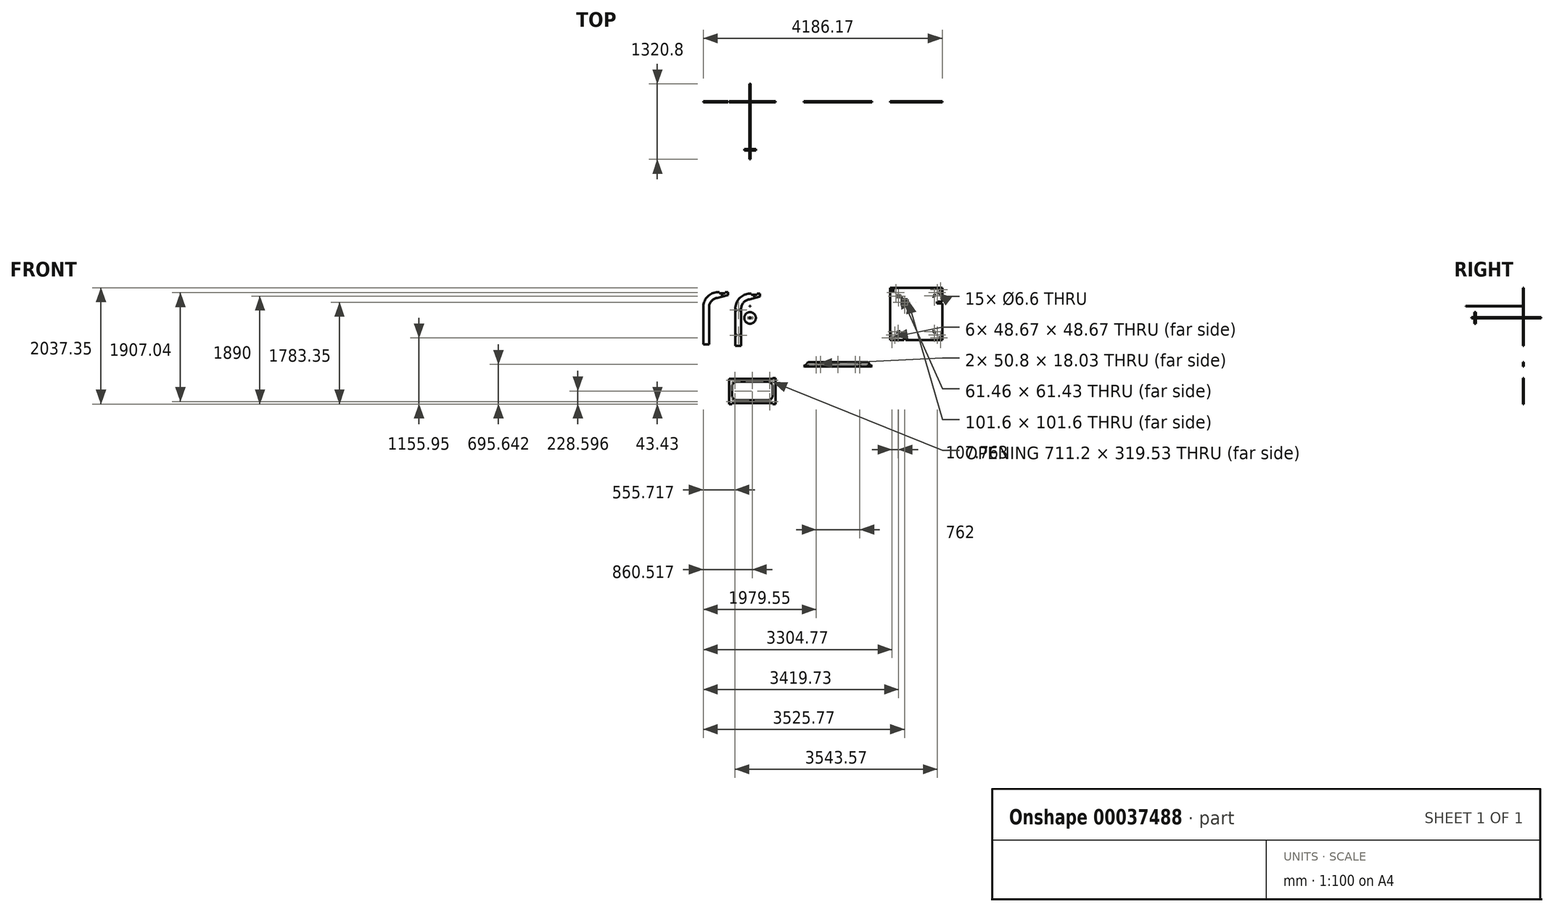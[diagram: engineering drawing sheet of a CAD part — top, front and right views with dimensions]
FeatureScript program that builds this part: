
annotation { "Feature Type Name" : "Feature", "Feature Type Description" : "" }
export const myFeature = defineFeature(function(context is Context, id is Id, definition is map)
    precondition{}
    {
        {
            var Q0;
            Q0=qCreatedBy(makeId("Front.planeOp"),FACE);
            var sketch = newSketch(context, id + "F0", { "sketchPlane" : qUnion([Q0])});
            skPoint(sketch, "E0.endSnap0", {"position": v(175.05, 374.22) * mm});
            skLineSegment(sketch, "E1", {"start": v(-256.75, -489.38) * mm, "end": v(-256.75, 159.86) * mm});
            skLineSegment(sketch, "E2", {"start": v(-13.2, 324.52) * mm, "end": v(175.05, 374.69) * mm});
            skLineSegment(sketch, "E3", {"start": v(-256.75, -489.38) * mm, "end": v(-155.15, -489.38) * mm});
            skArc(sketch, "E4.0", {"start": v(-13.2, 324.52) * mm, "mid": v(-114.76, 268.56) * mm, "end": v(-155.15, 159.86) * mm});
            skLineSegment(sketch, "E5", {"start": v(-155.15, -489.38) * mm, "end": v(-155.15, 159.86) * mm});
            skArc(sketch, "E6", {"start": v(-28.15, 425.02) * mm, "mid": v(-191.71, 334.9) * mm, "end": v(-256.75, 159.86) * mm});
            skLineSegment(sketch, "E0", {"start": v(-28.15, 374.69) * mm, "end": v(175.05, 374.69) * mm, "construction": true});
            skLineSegment(sketch, "E7", {"start": v(175.05, 406.98) * mm, "end": v(175.05, 341.45) * mm, "construction": true});
            skLineSegment(sketch, "E8", {"start": v(-28.15, 425.02) * mm, "end": v(22.65, 425.02) * mm});
            skLineSegment(sketch, "E9", {"start": v(175.05, 406.98) * mm, "end": v(175.05, 374.22) * mm});
            skLineSegment(sketch, "E10", {"start": v(22.65, 406.98) * mm, "end": v(124.25, 406.98) * mm});
            skLineSegment(sketch, "E11", {"start": v(175.05, 425.02) * mm, "end": v(175.05, 406.98) * mm});
            skLineSegment(sketch, "E12.MirrorCS", {"start": v(175.05, 425.02) * mm, "end": v(124.25, 425.02) * mm});
            skLineSegment(sketch, "E13", {"start": v(22.65, 425.02) * mm, "end": v(22.65, 406.98) * mm});
            skLineSegment(sketch, "E14.MirrorCS", {"start": v(124.25, 425.02) * mm, "end": v(124.25, 406.98) * mm});
            skLineSegment(sketch, "E15", {"start": v(-205.95, -489.38) * mm, "end": v(-205.95, -311.58) * mm, "construction": true});
            skPoint(sketch, "E15.endSnap0", {"position": v(-205.95, -489.38) * mm});
            skLineSegment(sketch, "E16.bottom", {"start": v(-256.75, 145.62) * mm, "end": v(-231.35, 145.62) * mm});
            skLineSegment(sketch, "E16.top", {"start": v(-256.75, 127.58) * mm, "end": v(-231.35, 127.58) * mm});
            skLineSegment(sketch, "E16.left", {"start": v(-256.75, 145.62) * mm, "end": v(-256.75, 127.58) * mm});
            skPoint(sketch, "E17.endSnap0", {"position": v(-388.49, 397.96) * mm});
            skArc(sketch, "E18.0", {"start": v(-576.73, 348.27) * mm, "mid": v(-678.3, 292.31) * mm, "end": v(-718.69, 183.6) * mm});
            skArc(sketch, "E19", {"start": v(-591.69, 448.76) * mm, "mid": v(-755.25, 358.65) * mm, "end": v(-820.29, 183.6) * mm});
            skLineSegment(sketch, "E20", {"start": v(-820.29, -465.64) * mm, "end": v(-820.29, 183.6) * mm});
            skPoint(sketch, "E21.endSnap0", {"position": v(-849.05, 398.3) * mm});
            skLineSegment(sketch, "E22", {"start": v(-718.69, -465.64) * mm, "end": v(-718.69, 183.6) * mm});
            skLineSegment(sketch, "E23", {"start": v(-576.73, 348.27) * mm, "end": v(-388.49, 398.43) * mm});
            skPoint(sketch, "E24.MirrorP", {"position": v(-490.09, 418.36) * mm});
            skLineSegment(sketch, "E25", {"start": v(-820.29, -465.64) * mm, "end": v(-718.69, -465.64) * mm});
            skLineSegment(sketch, "E17", {"start": v(-591.69, 398.43) * mm, "end": v(-388.49, 398.43) * mm, "construction": true});
            skLineSegment(sketch, "E26", {"start": v(-540.89, 430.73) * mm, "end": v(-439.29, 430.73) * mm});
            skLineSegment(sketch, "E27", {"start": v(-540.89, 448.76) * mm, "end": v(-540.89, 430.73) * mm});
            skLineSegment(sketch, "E28", {"start": v(-591.69, 448.76) * mm, "end": v(-540.89, 448.76) * mm});
            skLineSegment(sketch, "E29", {"start": v(-388.49, 448.76) * mm, "end": v(-388.49, 430.73) * mm});
            skLineSegment(sketch, "E30.MirrorCS", {"start": v(-388.49, 448.76) * mm, "end": v(-439.29, 448.76) * mm});
            skLineSegment(sketch, "E31", {"start": v(-388.49, 430.73) * mm, "end": v(-388.49, 365.2) * mm, "construction": true});
            skLineSegment(sketch, "E32", {"start": v(-388.49, 430.73) * mm, "end": v(-388.49, 397.96) * mm});
            skLineSegment(sketch, "E33.MirrorCS", {"start": v(-439.29, 448.76) * mm, "end": v(-439.29, 430.73) * mm});
            skCircle(sketch, "E34", {"center": v(-490.09, 405.33) * mm, "radius": 5.59 * mm});
            skLineSegment(sketch, "E35", {"start": v(-490.09, 399.74) * mm, "end": v(-490.09, 430.73) * mm, "construction": true});
            skLineSegment(sketch, "E36", {"start": v(-490.09, 398.43) * mm, "end": v(-490.09, 440.42) * mm, "construction": true});
            skLineSegment(sketch, "E37", {"start": v(-205.95, -489.38) * mm, "end": v(-205.95, -362.38) * mm, "construction": true});
            skLineSegment(sketch, "E38", {"start": v(-205.95, 76.78) * mm, "end": v(-205.95, -344.35) * mm, "construction": true});
            skCircle(sketch, "E39", {"center": v(73.45, 381.58) * mm, "radius": 5.59 * mm});
            skLineSegment(sketch, "E40", {"start": v(73.45, 376) * mm, "end": v(73.45, 406.98) * mm, "construction": true});
            skPoint(sketch, "E41", {"position": v(73.45, 406.98) * mm});
            skLineSegment(sketch, "E42.bottom", {"start": v(-366.17, -1069.77) * mm, "end": v(446.63, -1069.77) * mm});
            skLineSegment(sketch, "E42.top", {"start": v(-366.17, -1490.9) * mm, "end": v(446.63, -1490.9) * mm});
            skLineSegment(sketch, "E42.left", {"start": v(-366.17, -1069.77) * mm, "end": v(-366.17, -1490.9) * mm});
            skLineSegment(sketch, "E42.right", {"start": v(446.63, -1069.77) * mm, "end": v(446.63, -1490.9) * mm});
            skLineSegment(sketch, "E43.bottom", {"start": v(-366.17, -1069.77) * mm, "end": v(-315.37, -1069.77) * mm});
            skLineSegment(sketch, "E43.top", {"start": v(-366.17, -1051.73) * mm, "end": v(-315.37, -1051.73) * mm});
            skLineSegment(sketch, "E43.left", {"start": v(-366.17, -1069.77) * mm, "end": v(-366.17, -1051.73) * mm});
            skLineSegment(sketch, "E43.right", {"start": v(-315.37, -1069.77) * mm, "end": v(-315.37, -1051.73) * mm});
            skLineSegment(sketch, "E44", {"start": v(40.23, -1069.77) * mm, "end": v(40.23, -1490.9) * mm, "construction": true});
            skLineSegment(sketch, "E45", {"start": v(40.23, -1490.9) * mm, "end": v(446.63, -1280.33) * mm, "construction": true});
            skLineSegment(sketch, "E46", {"start": v(446.63, -1280.33) * mm, "end": v(-366.17, -1280.33) * mm, "construction": true});
            skLineSegment(sketch, "E47.MirrorCS", {"start": v(395.83, -1069.77) * mm, "end": v(395.83, -1051.73) * mm});
            skLineSegment(sketch, "E48.MirrorCS", {"start": v(446.63, -1069.77) * mm, "end": v(395.83, -1069.77) * mm});
            skLineSegment(sketch, "E49.MirrorCS", {"start": v(446.63, -1051.73) * mm, "end": v(395.83, -1051.73) * mm});
            skLineSegment(sketch, "E50.MirrorCS", {"start": v(446.63, -1069.77) * mm, "end": v(446.63, -1051.73) * mm});
            skLineSegment(sketch, "E51.MirrorCS", {"start": v(446.63, -1490.9) * mm, "end": v(446.63, -1508.93) * mm});
            skLineSegment(sketch, "E52.MirrorCS", {"start": v(-315.37, -1490.9) * mm, "end": v(-315.37, -1508.93) * mm});
            skLineSegment(sketch, "E53.MirrorCS", {"start": v(395.83, -1490.9) * mm, "end": v(395.83, -1508.93) * mm});
            skLineSegment(sketch, "E54.MirrorCS", {"start": v(-366.17, -1490.9) * mm, "end": v(-366.17, -1508.93) * mm});
            skLineSegment(sketch, "E55.MirrorCS", {"start": v(-366.17, -1508.93) * mm, "end": v(-315.37, -1508.93) * mm});
            skLineSegment(sketch, "E56.MirrorCS", {"start": v(446.63, -1490.9) * mm, "end": v(395.83, -1490.9) * mm});
            skLineSegment(sketch, "E57.MirrorCS", {"start": v(-366.17, -1490.9) * mm, "end": v(-315.37, -1490.9) * mm});
            skLineSegment(sketch, "E58.MirrorCS", {"start": v(446.63, -1508.93) * mm, "end": v(395.83, -1508.93) * mm});
            skLineSegment(sketch, "E59.bottom", {"start": v(-239.17, -1120.57) * mm, "end": v(319.63, -1120.57) * mm});
            skLineSegment(sketch, "E59.top", {"start": v(-239.17, -1440.1) * mm, "end": v(319.63, -1440.1) * mm});
            skLineSegment(sketch, "E59.left", {"start": v(-315.37, -1196.77) * mm, "end": v(-315.37, -1363.9) * mm});
            skLineSegment(sketch, "E59.right", {"start": v(395.83, -1196.77) * mm, "end": v(395.83, -1363.9) * mm});
            skPoint(sketch, "E60.visualSharp", {"position": v(-315.37, -1120.57) * mm});
            skArc(sketch, "E60.filletArc", {"start": v(-239.17, -1120.57) * mm, "mid": v(-293.05, -1142.89) * mm, "end": v(-315.37, -1196.77) * mm});
            skPoint(sketch, "E61.visualSharp", {"position": v(395.83, -1120.57) * mm});
            skArc(sketch, "E61.filletArc", {"start": v(395.83, -1196.77) * mm, "mid": v(373.5, -1142.89) * mm, "end": v(319.63, -1120.57) * mm});
            skPoint(sketch, "E62.visualSharp", {"position": v(395.83, -1440.1) * mm});
            skArc(sketch, "E62.filletArc", {"start": v(319.63, -1440.1) * mm, "mid": v(373.5, -1417.78) * mm, "end": v(395.83, -1363.9) * mm});
            skPoint(sketch, "E63.visualSharp", {"position": v(-315.37, -1440.1) * mm});
            skArc(sketch, "E63.filletArc", {"start": v(-315.37, -1363.9) * mm, "mid": v(-293.05, -1417.78) * mm, "end": v(-239.17, -1440.1) * mm});
            skLineSegment(sketch, "E64.right", {"start": v(2756.28, 325.22) * mm, "end": v(2756.28, 223.62) * mm});
            skLineSegment(sketch, "E65", {"start": v(2451.48, 71.22) * mm, "end": v(3365.88, 71.22) * mm, "construction": true});
            skLineSegment(sketch, "E66", {"start": v(3365.88, 71.22) * mm, "end": v(2908.68, 528.42) * mm, "construction": true});
            skLineSegment(sketch, "E67", {"start": v(2451.48, -385.98) * mm, "end": v(3365.88, 528.42) * mm, "construction": true});
            skLineSegment(sketch, "E68.trimOffspring", {"start": v(2728.84, -385.98) * mm, "end": v(3365.88, -385.98) * mm});
            skLineSegment(sketch, "E69.MirrorCS", {"start": v(3365.88, 286.32) * mm, "end": v(3270.63, 286.32) * mm});
            skLineSegment(sketch, "E70.bottom", {"start": v(2451.48, 528.42) * mm, "end": v(3365.88, 528.42) * mm});
            skLineSegment(sketch, "E70.top", {"start": v(2451.48, -385.98) * mm, "end": v(2693.91, -385.98) * mm});
            skLineSegment(sketch, "E71", {"start": v(2451.48, 528.42) * mm, "end": v(2451.48, 528.42) * mm});
            skLineSegment(sketch, "E70.left", {"start": v(2451.48, 528.42) * mm, "end": v(2451.48, -385.98) * mm});
            skLineSegment(sketch, "E70.right", {"start": v(3365.88, 528.42) * mm, "end": v(3365.88, 286.32) * mm});
            skLineSegment(sketch, "E64.top", {"start": v(2654.68, 223.62) * mm, "end": v(2756.28, 223.62) * mm});
            skLineSegment(sketch, "E72.MirrorCS", {"start": v(3270.63, 251.4) * mm, "end": v(3365.88, 251.4) * mm});
            skLineSegment(sketch, "E73", {"start": v(2451.48, 528.42) * mm, "end": v(3365.88, -385.98) * mm, "construction": true});
            skLineSegment(sketch, "E74.trimOffspring", {"start": v(3365.88, 251.4) * mm, "end": v(3365.88, -385.98) * mm});
            skLineSegment(sketch, "E75.right", {"start": v(2693.91, -386.78) * mm, "end": v(2693.91, -291.53) * mm});
            skLineSegment(sketch, "E64.left", {"start": v(2654.68, 325.22) * mm, "end": v(2654.68, 223.62) * mm});
            skPoint(sketch, "E76.orphan", {"position": v(2605.68, 387.29) * mm});
            skLineSegment(sketch, "E77.right", {"start": v(2728.84, -291.53) * mm, "end": v(2728.84, -385.98) * mm});
            skLineSegment(sketch, "E64.bottom", {"start": v(2654.68, 325.22) * mm, "end": v(2756.28, 325.22) * mm});
            skLineSegment(sketch, "E78.MirrorCS", {"start": v(2522.4, 483.62) * mm, "end": v(2486.49, 519.54) * mm});
            skLineSegment(sketch, "E79.MirrorCS", {"start": v(3270.63, 286.32) * mm, "end": v(3270.63, 251.4) * mm});
            skLineSegment(sketch, "E80.MirrorCS", {"start": v(2594.25, 411.78) * mm, "end": v(2630.17, 375.86) * mm});
            skLineSegment(sketch, "E81", {"start": v(2630.17, 375.86) * mm, "end": v(2604.67, 350.36) * mm});
            skLineSegment(sketch, "E82.MirrorCS", {"start": v(2522.4, 483.62) * mm, "end": v(2496.94, 458.08) * mm});
            skLineSegment(sketch, "E83.MirrorCS", {"start": v(2496.94, 458.08) * mm, "end": v(2460.98, 494.04) * mm});
            skLineSegment(sketch, "E84.MirrorCS", {"start": v(2568.71, 386.31) * mm, "end": v(2604.67, 350.36) * mm});
            skLineSegment(sketch, "E77.bottom", {"start": v(2693.91, -291.53) * mm, "end": v(2728.84, -291.53) * mm});
            skCircle(sketch, "E85", {"center": v(2551.8, 441.17) * mm, "radius": 3.3 * mm});
            skLineSegment(sketch, "E86", {"start": v(2594.25, 411.78) * mm, "end": v(2568.71, 386.31) * mm});
            skLineSegment(sketch, "E87", {"start": v(2612.2, 393.82) * mm, "end": v(2599.15, 380.76) * mm, "construction": true});
            skLineSegment(sketch, "E88", {"start": v(2587.7, 405.26) * mm, "end": v(2551.8, 441.17) * mm, "construction": true});
            skLineSegment(sketch, "E89", {"start": v(2551.8, 441.17) * mm, "end": v(2545.27, 434.64) * mm, "construction": true});
            skLineSegment(sketch, "E90.MirrorCS", {"start": v(2486.49, 519.54) * mm, "end": v(2460.98, 494.04) * mm});
            skLineSegment(sketch, "E91.MirrorCS", {"start": v(3212.14, 400.7) * mm, "end": v(3225.15, 387.7) * mm, "construction": true});
            skLineSegment(sketch, "E92.MirrorCS", {"start": v(3308.54, 483.84) * mm, "end": v(3344.47, 519.76) * mm});
            skLineSegment(sketch, "E93.MirrorCS", {"start": v(3236.7, 412) * mm, "end": v(3249.45, 399.24) * mm});
            skLineSegment(sketch, "E94.MirrorCS", {"start": v(3321.3, 471.08) * mm, "end": v(3357.22, 507) * mm});
            skLineSegment(sketch, "E95.MirrorCS", {"start": v(3249.45, 399.24) * mm, "end": v(3213.53, 363.32) * mm});
            skPoint(sketch, "E96.MirrorP", {"position": v(3218.65, 394.2) * mm});
            skLineSegment(sketch, "E97.MirrorCS", {"start": v(3344.47, 519.76) * mm, "end": v(3357.22, 507) * mm});
            skLineSegment(sketch, "E98.MirrorCS", {"start": v(3236.7, 412) * mm, "end": v(3200.78, 376.07) * mm});
            skLineSegment(sketch, "E99.MirrorCS", {"start": v(3200.78, 376.07) * mm, "end": v(3213.53, 363.32) * mm});
            skLineSegment(sketch, "E100.MirrorCS", {"start": v(3308.54, 483.84) * mm, "end": v(3321.3, 471.08) * mm});
            skLineSegment(sketch, "E101", {"start": v(2908.68, 528.42) * mm, "end": v(2908.68, -385.98) * mm, "construction": true});
            skPoint(sketch, "E102", {"position": v(3314.92, 477.46) * mm});
            skLineSegment(sketch, "E103", {"start": v(-532.03, -811.57) * mm, "end": v(-532.06, -805.22) * mm});
            skLineSegment(sketch, "E104.0", {"start": v(-366.17, -1095.17) * mm, "end": v(446.63, -1095.17) * mm, "construction": true});
            skCircle(sketch, "E105", {"center": v(40.23, -1095.17) * mm, "radius": 3.3 * mm});
            skCircle(sketch, "E106", {"center": v(-264.57, -1095.17) * mm, "radius": 3.3 * mm});
            skCircle(sketch, "E107.MirrorC", {"center": v(345.03, -1095.17) * mm, "radius": 3.3 * mm});
            skPoint(sketch, "E108", {"position": v(1184.66, -813.29) * mm});
            skLineSegment(sketch, "E109", {"start": v(949.71, -849.2) * mm, "end": v(2130.8, -849.2) * mm});
            skLineSegment(sketch, "E110", {"start": v(2058.96, -777.37) * mm, "end": v(1021.55, -777.37) * mm});
            skLineSegment(sketch, "E111.bottom", {"start": v(1133.86, -822.3) * mm, "end": v(1184.66, -822.3) * mm});
            skLineSegment(sketch, "E111.top", {"start": v(1133.86, -804.27) * mm, "end": v(1184.66, -804.27) * mm});
            skLineSegment(sketch, "E112", {"start": v(1540.26, -849.2) * mm, "end": v(1540.26, -777.37) * mm, "construction": true});
            skLineSegment(sketch, "E113", {"start": v(949.71, -849.2) * mm, "end": v(1021.55, -777.37) * mm});
            skCircle(sketch, "E114", {"center": v(1235.46, -813.29) * mm, "radius": 3.3 * mm});
            skLineSegment(sketch, "E111.right", {"start": v(1184.66, -822.3) * mm, "end": v(1184.66, -804.27) * mm});
            skLineSegment(sketch, "E111.left", {"start": v(1133.86, -822.3) * mm, "end": v(1133.86, -804.27) * mm});
            skLineSegment(sketch, "E115.MirrorCS", {"start": v(2130.8, -849.2) * mm, "end": v(2058.96, -777.37) * mm});
            skCircle(sketch, "E116.MirrorC", {"center": v(3279, 441.54) * mm, "radius": 3.3 * mm});
            skLineSegment(sketch, "E117", {"start": v(3243.08, 405.62) * mm, "end": v(3314.92, 477.46) * mm, "construction": true});
            skCircle(sketch, "E118.MirrorC", {"center": v(3279, -299.1) * mm, "radius": 3.3 * mm});
            skLineSegment(sketch, "E119.MirrorCS", {"start": v(3236.7, -269.55) * mm, "end": v(3249.45, -256.8) * mm});
            skLineSegment(sketch, "E120.MirrorCS", {"start": v(3344.47, -377.31) * mm, "end": v(3357.22, -364.56) * mm});
            skLineSegment(sketch, "E121.MirrorCS", {"start": v(3308.54, -341.4) * mm, "end": v(3321.3, -328.64) * mm});
            skLineSegment(sketch, "E122.MirrorCS", {"start": v(3200.78, -233.63) * mm, "end": v(3213.53, -220.88) * mm});
            skLineSegment(sketch, "E123.MirrorCS", {"start": v(3243.08, -263.17) * mm, "end": v(3314.92, -335.02) * mm, "construction": true});
            skLineSegment(sketch, "E124.MirrorCS", {"start": v(3212.14, -258.26) * mm, "end": v(3225.15, -245.25) * mm, "construction": true});
            skLineSegment(sketch, "E125.MirrorCS", {"start": v(3321.3, -328.64) * mm, "end": v(3357.22, -364.56) * mm});
            skLineSegment(sketch, "E126.MirrorCS", {"start": v(3236.7, -269.55) * mm, "end": v(3200.78, -233.63) * mm});
            skLineSegment(sketch, "E127.MirrorCS", {"start": v(3308.54, -341.4) * mm, "end": v(3344.47, -377.31) * mm});
            skPoint(sketch, "E128.MirrorP", {"position": v(3218.65, -251.76) * mm});
            skPoint(sketch, "E129.MirrorP", {"position": v(3314.92, -335.02) * mm});
            skLineSegment(sketch, "E130.MirrorCS", {"start": v(3249.45, -256.8) * mm, "end": v(3213.53, -220.88) * mm});
            skLineSegment(sketch, "E131.MirrorCS", {"start": v(2508.82, -341.4) * mm, "end": v(2496.07, -328.64) * mm});
            skCircle(sketch, "E132.MirrorC", {"center": v(2538.37, -299.1) * mm, "radius": 3.3 * mm});
            skLineSegment(sketch, "E133.MirrorCS", {"start": v(2616.58, -233.63) * mm, "end": v(2603.83, -220.88) * mm});
            skLineSegment(sketch, "E134.MirrorCS", {"start": v(2580.66, -269.55) * mm, "end": v(2567.91, -256.8) * mm});
            skLineSegment(sketch, "E135.MirrorCS", {"start": v(2472.9, -377.31) * mm, "end": v(2460.15, -364.56) * mm});
            skLineSegment(sketch, "E136.MirrorCS", {"start": v(2580.66, -269.55) * mm, "end": v(2616.58, -233.63) * mm});
            skLineSegment(sketch, "E137.MirrorCS", {"start": v(2567.91, -256.8) * mm, "end": v(2603.83, -220.88) * mm});
            skLineSegment(sketch, "E138.MirrorCS", {"start": v(2574.29, -263.17) * mm, "end": v(2502.44, -335.02) * mm, "construction": true});
            skLineSegment(sketch, "E139.MirrorCS", {"start": v(2605.22, -258.26) * mm, "end": v(2592.21, -245.25) * mm, "construction": true});
            skLineSegment(sketch, "E140.MirrorCS", {"start": v(2496.07, -328.64) * mm, "end": v(2460.15, -364.56) * mm});
            skPoint(sketch, "E141.MirrorP", {"position": v(2598.72, -251.76) * mm});
            skLineSegment(sketch, "E142.MirrorCS", {"start": v(2508.82, -341.4) * mm, "end": v(2472.9, -377.31) * mm});
            skPoint(sketch, "E143.MirrorP", {"position": v(2502.44, -335.02) * mm});
            skPoint(sketch, "E144", {"position": v(1540.26, -777.37) * mm});
            skLineSegment(sketch, "E145", {"start": v(1184.66, -813.29) * mm, "end": v(1235.46, -813.29) * mm, "construction": true});
            skLineSegment(sketch, "E146", {"start": v(1184.66, -813.29) * mm, "end": v(1540.26, -813.29) * mm, "construction": true});
            skPoint(sketch, "E147", {"position": v(1540.26, -813.29) * mm});
            skLineSegment(sketch, "E148.bottom", {"start": v(1021.55, -777.37) * mm, "end": v(949.71, -777.37) * mm, "construction": true});
            skLineSegment(sketch, "E148.top", {"start": v(1021.55, -849.2) * mm, "end": v(949.71, -849.2) * mm, "construction": true});
            skLineSegment(sketch, "E148.left", {"start": v(1021.55, -777.37) * mm, "end": v(1021.55, -849.2) * mm, "construction": true});
            skLineSegment(sketch, "E148.right", {"start": v(949.71, -777.37) * mm, "end": v(949.71, -849.2) * mm, "construction": true});
            skLineSegment(sketch, "E149.MirrorCS", {"start": v(1946.66, -822.3) * mm, "end": v(1946.66, -804.27) * mm});
            skLineSegment(sketch, "E150.MirrorCS", {"start": v(1895.86, -822.3) * mm, "end": v(1895.86, -804.27) * mm});
            skCircle(sketch, "E151.MirrorC", {"center": v(1845.06, -813.29) * mm, "radius": 3.3 * mm});
            skLineSegment(sketch, "E152.MirrorCS", {"start": v(1946.66, -804.27) * mm, "end": v(1895.86, -804.27) * mm});
            skLineSegment(sketch, "E153.MirrorCS", {"start": v(1946.66, -822.3) * mm, "end": v(1895.86, -822.3) * mm});
            skLineSegment(sketch, "E154.MirrorCS", {"start": v(1895.86, -813.29) * mm, "end": v(1845.06, -813.29) * mm, "construction": true});
            skPoint(sketch, "E155.MirrorP", {"position": v(1895.86, -813.29) * mm});
            skCircle(sketch, "E156", {"center": v(1540.26, -813.29) * mm, "radius": 3.3 * mm});
            skLineSegment(sketch, "E157", {"start": v(985.63, -813.29) * mm, "end": v(949.71, -777.37) * mm, "construction": true});
            skLineSegment(sketch, "E158", {"start": v(949.71, -849.2) * mm, "end": v(944.68, -844.18) * mm});
            skLineSegment(sketch, "E159", {"start": v(944.68, -844.18) * mm, "end": v(962.64, -826.22) * mm});
            skLineSegment(sketch, "E160", {"start": v(962.64, -826.22) * mm, "end": v(967.67, -831.25) * mm});
            skLineSegment(sketch, "E161.MirrorCS", {"start": v(1021.55, -777.37) * mm, "end": v(1016.52, -772.34) * mm});
            skLineSegment(sketch, "E162.MirrorCS", {"start": v(1016.52, -772.34) * mm, "end": v(998.56, -790.3) * mm});
            skLineSegment(sketch, "E163.MirrorCS", {"start": v(998.56, -790.3) * mm, "end": v(1003.6, -795.33) * mm});
            skLineSegment(sketch, "E164", {"start": v(-205.95, 127.58) * mm, "end": v(-205.95, -293.55) * mm, "construction": true});
            skLineSegment(sketch, "E165", {"start": v(-205.95, -82.98) * mm, "end": v(-295.54, -82.98) * mm, "construction": true});
            skLineSegment(sketch, "E166", {"start": v(-231.35, 145.62) * mm, "end": v(-231.35, 127.58) * mm});
            skLineSegment(sketch, "E167.MirrorCS", {"start": v(-155.15, 127.58) * mm, "end": v(-180.55, 127.58) * mm});
            skLineSegment(sketch, "E168.MirrorCS", {"start": v(-180.55, 145.62) * mm, "end": v(-180.55, 127.58) * mm});
            skLineSegment(sketch, "E169.MirrorCS", {"start": v(-155.15, 145.62) * mm, "end": v(-155.15, 127.58) * mm});
            skLineSegment(sketch, "E170.MirrorCS", {"start": v(-155.15, 145.62) * mm, "end": v(-180.55, 145.62) * mm});
            skLineSegment(sketch, "E171.MirrorCS", {"start": v(-231.35, -311.58) * mm, "end": v(-231.35, -293.55) * mm});
            skLineSegment(sketch, "E172.MirrorCS", {"start": v(-256.75, -311.58) * mm, "end": v(-256.75, -293.55) * mm});
            skLineSegment(sketch, "E173.MirrorCS", {"start": v(-256.75, -311.58) * mm, "end": v(-231.35, -311.58) * mm});
            skLineSegment(sketch, "E174.MirrorCS", {"start": v(-155.15, -311.58) * mm, "end": v(-155.15, -293.55) * mm});
            skLineSegment(sketch, "E175.MirrorCS", {"start": v(-155.15, -293.55) * mm, "end": v(-180.55, -293.55) * mm});
            skLineSegment(sketch, "E176.MirrorCS", {"start": v(-155.15, -311.58) * mm, "end": v(-180.55, -311.58) * mm});
            skLineSegment(sketch, "E177.MirrorCS", {"start": v(-180.55, -311.58) * mm, "end": v(-180.55, -293.55) * mm});
            skLineSegment(sketch, "E178.MirrorCS", {"start": v(-256.75, -293.55) * mm, "end": v(-231.35, -293.55) * mm});
            skLineSegment(sketch, "E179.MirrorCS", {"start": v(2130.8, -849.2) * mm, "end": v(2135.83, -844.18) * mm});
            skLineSegment(sketch, "E180.MirrorCS", {"start": v(2135.83, -844.18) * mm, "end": v(2117.87, -826.22) * mm});
            skLineSegment(sketch, "E181.MirrorCS", {"start": v(2117.87, -826.22) * mm, "end": v(2112.84, -831.25) * mm});
            skLineSegment(sketch, "E182.MirrorCS", {"start": v(2058.96, -777.37) * mm, "end": v(2063.99, -772.34) * mm});
            skLineSegment(sketch, "E183.MirrorCS", {"start": v(2081.95, -790.3) * mm, "end": v(2076.92, -795.33) * mm});
            skLineSegment(sketch, "E184.MirrorCS", {"start": v(2063.99, -772.34) * mm, "end": v(2081.95, -790.3) * mm});
            skLineSegment(sketch, "E185", {"start": v(985.1, -803.77) * mm, "end": v(1008.08, -826.76) * mm, "construction": true});
            skCircle(sketch, "E186", {"center": v(1008.08, -826.76) * mm, "radius": 5.59 * mm});
            skCircle(sketch, "E187.MirrorC", {"center": v(2072.43, -826.76) * mm, "radius": 5.59 * mm});
            skCircle(sketch, "E188.MirrorC", {"center": v(40.23, -1465.5) * mm, "radius": 3.3 * mm});
            skCircle(sketch, "E189.MirrorC", {"center": v(-264.57, -1465.5) * mm, "radius": 3.3 * mm});
            skCircle(sketch, "E190.MirrorC", {"center": v(345.03, -1465.5) * mm, "radius": 3.3 * mm});
            skLineSegment(sketch, "E191", {"start": v(-180.55, 136.6) * mm, "end": v(-199.6, 136.6) * mm, "construction": true});
            skCircle(sketch, "E192", {"center": v(-199.6, 136.6) * mm, "radius": 3.3 * mm});
            skLineSegment(sketch, "E193", {"start": v(998.56, -790.3) * mm, "end": v(985.1, -803.77) * mm, "construction": true});
            skCircle(sketch, "E194.MirrorC", {"center": v(-199.6, -302.57) * mm, "radius": 3.3 * mm});
            skCircle(sketch, "E195", {"center": v(0, 0) * mm, "radius": 9.53 * mm});
            skLineSegment(sketch, "E196.bottom", {"start": v(-44.45, 15.88) * mm, "end": v(44.45, 15.88) * mm});
            skLineSegment(sketch, "E196.top", {"start": v(-44.45, -15.88) * mm, "end": v(44.45, -15.88) * mm});
            skLineSegment(sketch, "E196.left", {"start": v(-44.45, 15.88) * mm, "end": v(-44.45, -15.88) * mm});
            skLineSegment(sketch, "E196.right", {"start": v(44.45, 15.88) * mm, "end": v(44.45, -15.88) * mm});
            skLineSegment(sketch, "E197.bottom", {"start": v(-11.11, 207) * mm, "end": v(11.11, 207) * mm});
            skLineSegment(sketch, "E197.top", {"start": v(-11.11, 199.4) * mm, "end": v(11.11, 199.4) * mm});
            skLineSegment(sketch, "E197.left", {"start": v(-11.11, 207) * mm, "end": v(-11.11, 199.4) * mm});
            skLineSegment(sketch, "E197.right", {"start": v(11.11, 207) * mm, "end": v(11.11, 199.4) * mm});
            skPoint(sketch, "E197.middle", {"position": v(0, 203.2) * mm});
            skSolve(sketch);
        }
        {
            var Q0;
            Q0=makeQuery(id+"F0.imprint","IMPRINT",FACE,{"disambiguationData":[TD([[makeQuery(id+"F0.imprint","IMPRINT",EDGE,{"derivedFrom":sQuery(id+"F0.wireOp",EDGE,"b7191b00-89fe-449c-a412-d32c6dc7ca24")}),-1.0]])]});
            var Q1;
            Q1=makeQuery(id+"F0.imprint","IMPRINT",FACE,{"disambiguationData":[TD([[makeQuery(id+"F0.imprint","IMPRINT",EDGE,{"derivedFrom":sQuery(id+"F0.wireOp",EDGE,"2d5de39e-6a3a-4305-85b2-5a3cd898bd56.bottom")}),-1.0]])]});
            var Q2;
            Q2=makeQuery(id+"F0.imprint","IMPRINT",FACE,{"disambiguationData":[TD([[makeQuery(id+"F0.imprint","IMPRINT",EDGE,{"derivedFrom":sQuery(id+"F0.wireOp",EDGE,"52b04602-891c-4f0b-9f4b-30c39f058121")}),1.0]])]});
            var Q3;
            Q3=makeQuery(id+"F0.imprint","IMPRINT",FACE,{"disambiguationData":[TD([[makeQuery(id+"F0.imprint","IMPRINT",EDGE,{"derivedFrom":sQuery(id+"F0.wireOp",EDGE,"e6eb8baf-ef0b-4c92-a250-6a5ced1377bc")}),1.0]])]});
            var Q4;
            Q4=makeQuery(id+"F0.imprint","IMPRINT",FACE,{"disambiguationData":[TD([[makeQuery(id+"F0.imprint","IMPRINT",EDGE,{"derivedFrom":sQuery(id+"F0.wireOp",EDGE,"E1")}),-1.0]])]});
            var Q5;
            Q5=makeQuery(id+"F0.imprint","IMPRINT",FACE,{"disambiguationData":[TD([[makeQuery(id+"F0.imprint","IMPRINT",EDGE,{"derivedFrom":sQuery(id+"F0.wireOp",EDGE,"E18.0")}),-1.0]])]});
            var Q6;
            Q6=makeQuery(id+"F0.imprint","IMPRINT",FACE,{"disambiguationData":[TD([[makeQuery(id+"F0.imprint","IMPRINT",EDGE,{"derivedFrom":sQuery(id+"F0.wireOp",EDGE,"60dec60a-5e68-4974-9949-9d8ab2d2e04c")}),1.0]])]});
            var Q7;
            {var subQ5=sQuery(id+"F0.wireOp",EDGE,"5e668abd-782b-45f1-970a-bf8f7c6f1287");Q7=makeQuery(id+"F0.imprint","IMPRINT",FACE,{"disambiguationData":[TD([[makeQuery(id+"F0.imprint","IMPRINT",EDGE,{"derivedFrom":subQ5}),-1.0]])]});}
            var Q8;
            Q8=makeQuery(id+"F0.imprint","IMPRINT",FACE,{"disambiguationData":[TD([[makeQuery(id+"F0.imprint","IMPRINT",EDGE,{"derivedFrom":sQuery(id+"F0.wireOp",EDGE,"5cd51394-2898-4257-be62-46ee7a2a2e3a")}),1.0]])]});
            var Q9;
            {var subQ2=sQuery(id+"F0.wireOp",EDGE,"41bdd055-ea06-4390-9998-cc3cb89cc6072.MirrorCS");Q9=makeQuery(id+"F0.imprint","IMPRINT",FACE,{"disambiguationData":[TD([[makeQuery(id+"F0.imprint","IMPRINT",EDGE,{"derivedFrom":subQ2}),-1.0]])]});}
            var Q10;
            {var subQ2=sQuery(id+"F0.wireOp",EDGE,"41bdd055-ea06-4390-9998-cc3cb89cc6070.MirrorCS");Q10=makeQuery(id+"F0.imprint","IMPRINT",FACE,{"disambiguationData":[TD([[makeQuery(id+"F0.imprint","IMPRINT",EDGE,{"derivedFrom":subQ2}),1.0]])]});}
            var Q11;
            Q11=makeQuery(id+"F0.imprint","IMPRINT",FACE,{"disambiguationData":[TD([[makeQuery(id+"F0.imprint","IMPRINT",EDGE,{"derivedFrom":sQuery(id+"F0.wireOp",EDGE,"49f6f6fd-91ff-4c82-a904-643047193003")}),1.0]])]});
            var Q12;
            {var subQ6=sQuery(id+"F0.wireOp",EDGE,"E42.left");Q12=makeQuery(id+"F0.imprint","IMPRINT",FACE,{"disambiguationData":[TD([[makeQuery(id+"F0.imprint","IMPRINT",EDGE,{"derivedFrom":subQ6}),1.0]])]});}
            var Q13;
            Q13=makeQuery(id+"F0.imprint","IMPRINT",FACE,{"disambiguationData":[TD([[makeQuery(id+"F0.imprint","IMPRINT",EDGE,{"derivedFrom":sQuery(id+"F0.wireOp",EDGE,"E43.bottom")}),1.0]])]});
            var Q14;
            Q14=makeQuery(id+"F0.imprint","IMPRINT",FACE,{"disambiguationData":[TD([[makeQuery(id+"F0.imprint","IMPRINT",EDGE,{"derivedFrom":sQuery(id+"F0.wireOp",EDGE,"E47.MirrorCS")}),-1.0]])]});
            var Q15;
            Q15=makeQuery(id+"F0.imprint","IMPRINT",FACE,{"disambiguationData":[TD([[makeQuery(id+"F0.imprint","IMPRINT",EDGE,{"derivedFrom":sQuery(id+"F0.wireOp",EDGE,"E51.MirrorCS")}),-1.0]])]});
            var Q16;
            Q16=makeQuery(id+"F0.imprint","IMPRINT",FACE,{"disambiguationData":[TD([[makeQuery(id+"F0.imprint","IMPRINT",EDGE,{"derivedFrom":sQuery(id+"F0.wireOp",EDGE,"E52.MirrorCS")}),-1.0]])]});
            var Q17;
            Q17=makeQuery(id+"F0.imprint","IMPRINT",FACE,{"disambiguationData":[TD([[makeQuery(id+"F0.imprint","IMPRINT",EDGE,{"derivedFrom":sQuery(id+"F0.wireOp",EDGE,"E64.right")}),1.0]])]});
            var Q18;
            {var subQ4=sQuery(id+"F0.wireOp",EDGE,"E109");Q18=makeQuery(id+"F0.imprint","IMPRINT",FACE,{"disambiguationData":[TD([[makeQuery(id+"F0.imprint","IMPRINT",EDGE,{"derivedFrom":subQ4}),1.0]])]});}
            var Q19;
            Q19=makeQuery(id+"F0.imprint","IMPRINT",FACE,{"disambiguationData":[TD([[makeQuery(id+"F0.imprint","IMPRINT",EDGE,{"derivedFrom":sQuery(id+"F0.wireOp",EDGE,"8675048f-54b9-41c1-bf46-67bb9466c1e5")}),1.0]])]});
            var Q20;
            {var subQ0=sQuery(id+"F0.wireOp",EDGE,"991999f0-6855-4b8c-9ef3-4de596fc9bac1.MirrorCS");Q20=makeQuery(id+"F0.imprint","IMPRINT",FACE,{"disambiguationData":[TD([[makeQuery(id+"F0.imprint","IMPRINT",EDGE,{"derivedFrom":subQ0}),-1.0]])]});}
            var Q21;
            {var subQ0=sQuery(id+"F0.wireOp",EDGE,"E158");Q21=makeQuery(id+"F0.imprint","IMPRINT",FACE,{"disambiguationData":[TD([[makeQuery(id+"F0.imprint","IMPRINT",EDGE,{"derivedFrom":subQ0}),-1.0]])]});}
            var Q22;
            {var subQ0=sQuery(id+"F0.wireOp",EDGE,"E161.MirrorCS");Q22=makeQuery(id+"F0.imprint","IMPRINT",FACE,{"disambiguationData":[TD([[makeQuery(id+"F0.imprint","IMPRINT",EDGE,{"derivedFrom":subQ0}),1.0]])]});}
            var Q23;
            {var subQ0=sQuery(id+"F0.wireOp",EDGE,"E182.MirrorCS");Q23=makeQuery(id+"F0.imprint","IMPRINT",FACE,{"disambiguationData":[TD([[makeQuery(id+"F0.imprint","IMPRINT",EDGE,{"derivedFrom":subQ0}),-1.0]])]});}
            var Q24;
            {var subQ0=sQuery(id+"F0.wireOp",EDGE,"E179.MirrorCS");Q24=makeQuery(id+"F0.imprint","IMPRINT",FACE,{"disambiguationData":[TD([[makeQuery(id+"F0.imprint","IMPRINT",EDGE,{"derivedFrom":subQ0}),1.0]])]});}
            var Q25;
            Q25=makeQuery(id+"F0.imprint","IMPRINT",FACE,{"disambiguationData":[TD([[makeQuery(id+"F0.imprint","IMPRINT",EDGE,{"derivedFrom":sQuery(id+"F0.wireOp",EDGE,"E195")}),-1.0]])]});
            extrude(context, id + "F1", {"entities" : qUnion([Q0, Q1, Q2, Q3, Q4, Q5, Q6, Q7, Q8, Q9, Q10, Q11, Q12, Q13, Q14, Q15, Q16, Q17, Q18, Q19, Q20, Q21, Q22, Q23, Q24, Q25]), "depth" : 18.03 * mm});
        }
        {
            var Q0;
            Q0=makeQuery(id+"F0.imprint","IMPRINT",FACE,{"disambiguationData":[TD([[makeQuery(id+"F0.imprint","IMPRINT",EDGE,{"derivedFrom":sQuery(id+"F0.wireOp",EDGE,"E197.bottom")}),-1.0]])]});
            extrude(context, id + "F2", {"entities" : qUnion([Q0]), "depth" : 1016 * mm});
        }
        {
            var Q0;
            Q0=makeQuery(id+"F0.imprint","IMPRINT",FACE,{"disambiguationData":[TD([[makeQuery(id+"F0.imprint","IMPRINT",EDGE,{"derivedFrom":sQuery(id+"F0.wireOp",EDGE,"E195")}),1.0]])]});
            extrude(context, id + "F3", {"entities" : qUnion([Q0]), "operationType" : NewBodyOperationType.ADD, "depth" : 914.4 * mm, "hasSecondDirection" : true, "secondDirectionOppositeDirection" : true, "secondDirectionDepth" : 304.8 * mm});
        }
        {
            var Q0;
            Q0=makeQuery(id+"F3.opExtrude","CAP_FACE",FACE,{"disambiguationData":[OSD([sQuery(id+"F0.wireOp",EDGE,"E195")])],"isStart":false});
            var sketch = newSketch(context, id + "F4", { "sketchPlane" : qUnion([Q0])});
            skCircle(sketch, "E198", {"center": v(0, 0) * mm, "radius": 101.6 * mm});
            skSolve(sketch);
        }
        {
            var Q0;
            Q0=makeQuery(id+"F4.imprint","IMPRINT",FACE,{"disambiguationData":[TD([[makeQuery(id+"F4.imprint","IMPRINT",EDGE,{"derivedFrom":sQuery(id+"F4.wireOp",EDGE,"E198")}),1.0]])]});
            extrude(context, id + "F5", {"entities" : qUnion([Q0]), "operationType" : NewBodyOperationType.ADD, "oppositeDirection" : true, "depth" : 76.2 * mm, "hasSecondDirection" : true, "secondDirectionOppositeDirection" : true, "secondDirectionDepth" : 50.8 * mm});
        }
    });
